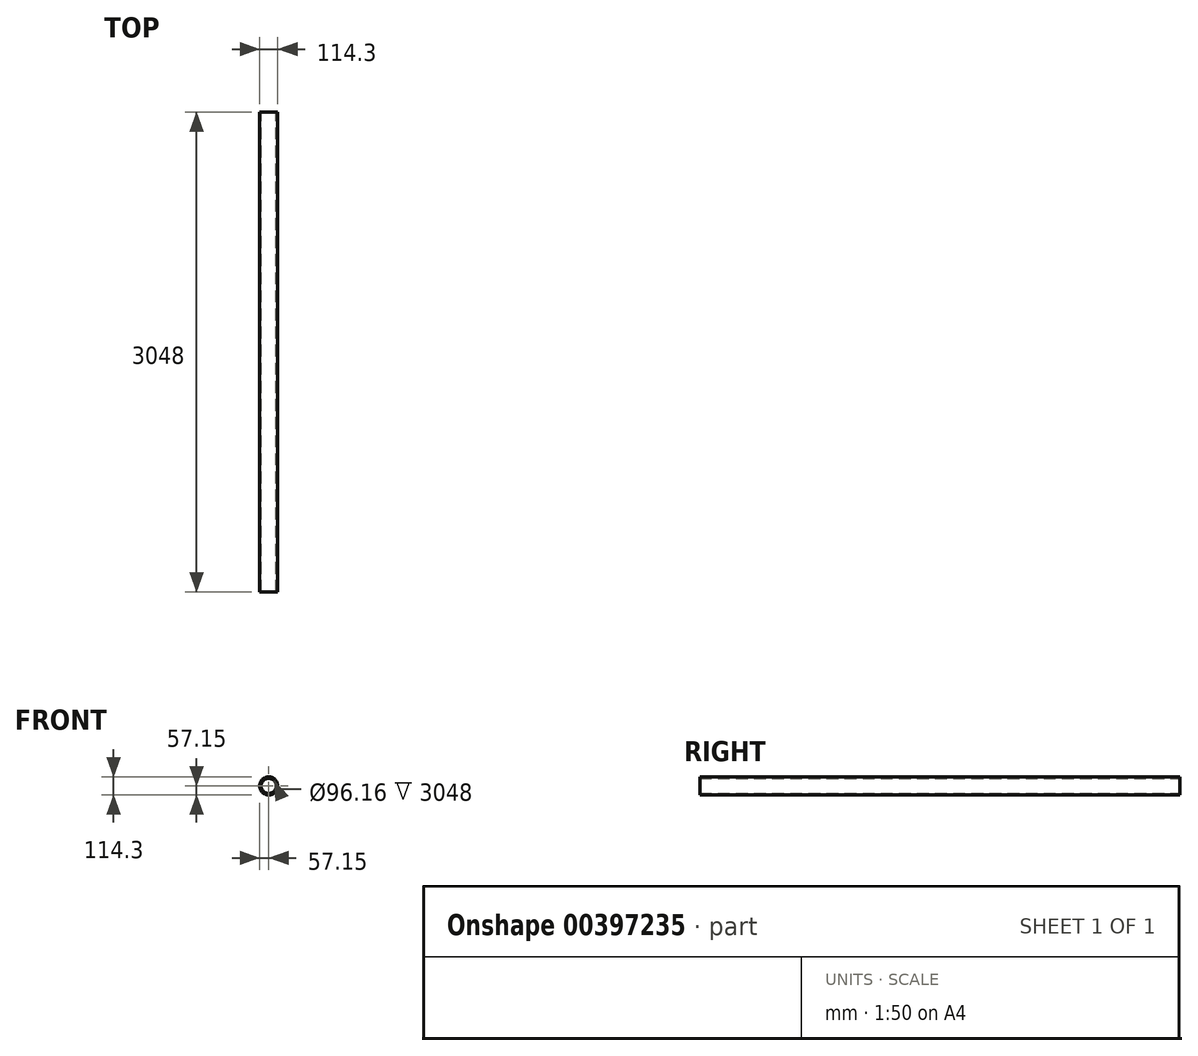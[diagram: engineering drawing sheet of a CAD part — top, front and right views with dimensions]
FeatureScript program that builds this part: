
annotation { "Feature Type Name" : "Feature", "Feature Type Description" : "" }
export const myFeature = defineFeature(function(context is Context, id is Id, definition is map)
    precondition{}
    {
        {
            var Q0;
            Q0=qCreatedBy(makeId("Front.planeOp"),FACE);
            var sketch = newSketch(context, id + "F0", { "sketchPlane" : qUnion([Q0])});
            skCircle(sketch, "E0", {"center": v(0, 0) * mm, "radius": 57.15 * mm});
            skCircle(sketch, "E1", {"center": v(0, 0) * mm, "radius": 48.08 * mm});
            skSolve(sketch);
        }
        {
            var Q0;
            Q0=qSketchRegion(id+"F0",true);
            extrude(context, id + "F1", {"entities" : qUnion([Q0]), "depth" : 3048 * mm});
        }
        {
            var Q0;
            Q0=qCreatedBy(makeId("Front.planeOp"),FACE);
            var sketch = newSketch(context, id + "F2", { "sketchPlane" : qUnion([Q0])});
            skLineSegment(sketch, "E2", {"start": v(0, 0) * mm, "end": v(-96.2, 0) * mm, "construction": true});
            skSolve(sketch);
        }
    });
